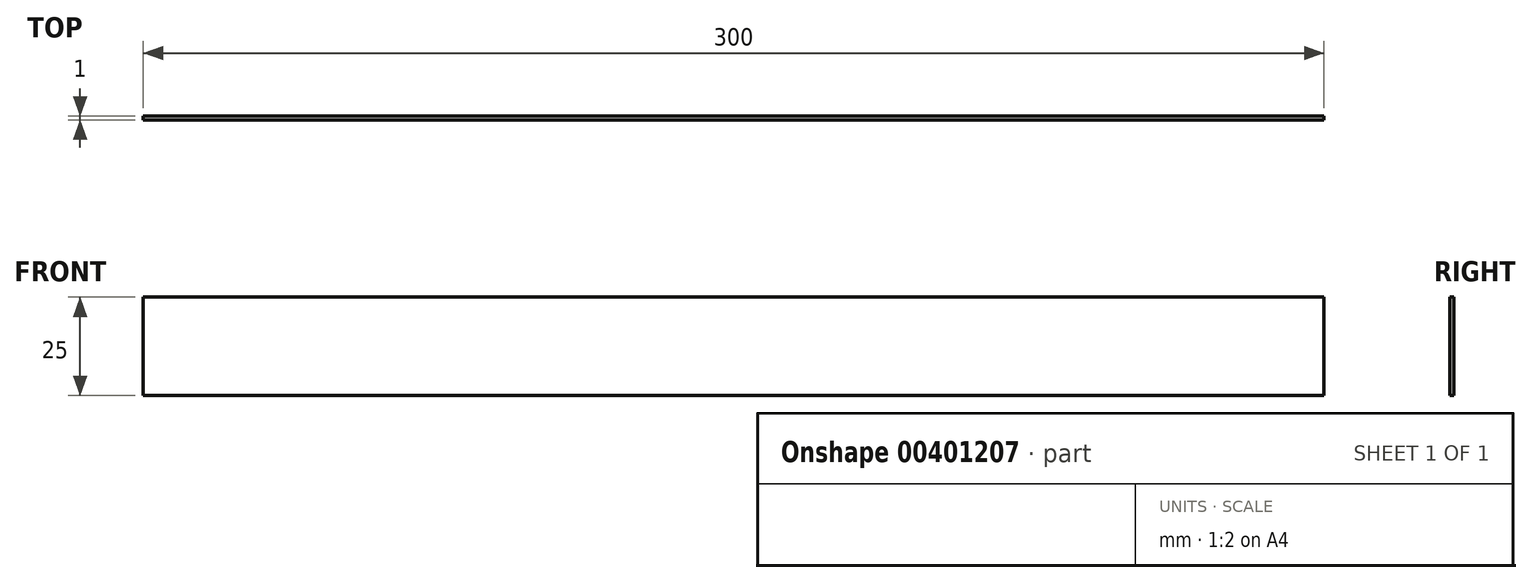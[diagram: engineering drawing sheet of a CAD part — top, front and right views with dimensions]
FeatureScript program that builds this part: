
annotation { "Feature Type Name" : "Feature", "Feature Type Description" : "" }
export const myFeature = defineFeature(function(context is Context, id is Id, definition is map)
    precondition{}
    {
        {
            var Q0;
            Q0=qCreatedBy(makeId("Front.planeOp"),FACE);
            var sketch = newSketch(context, id + "F0", { "sketchPlane" : qUnion([Q0])});
            skLineSegment(sketch, "E0.bottom", {"start": v(150, 12.5) * mm, "end": v(-150, 12.5) * mm});
            skLineSegment(sketch, "E0.top", {"start": v(150, -12.5) * mm, "end": v(-150, -12.5) * mm});
            skLineSegment(sketch, "E0.left", {"start": v(150, 12.5) * mm, "end": v(150, -12.5) * mm});
            skLineSegment(sketch, "E0.right", {"start": v(-150, 12.5) * mm, "end": v(-150, -12.5) * mm});
            skPoint(sketch, "E0.middle", {"position": v(0, 0) * mm});
            skSolve(sketch);
        }
        {
            var Q0;
            Q0=makeQuery(id+"F0.imprint","IMPRINT",FACE,{"disambiguationData":[TD([[makeQuery(id+"F0.imprint","IMPRINT",EDGE,{"derivedFrom":sQuery(id+"F0.wireOp",EDGE,"E0.bottom")}),1.0]])]});
            extrude(context, id + "F1", {"entities" : qUnion([Q0]), "depth" : 1 * mm});
        }
    });
